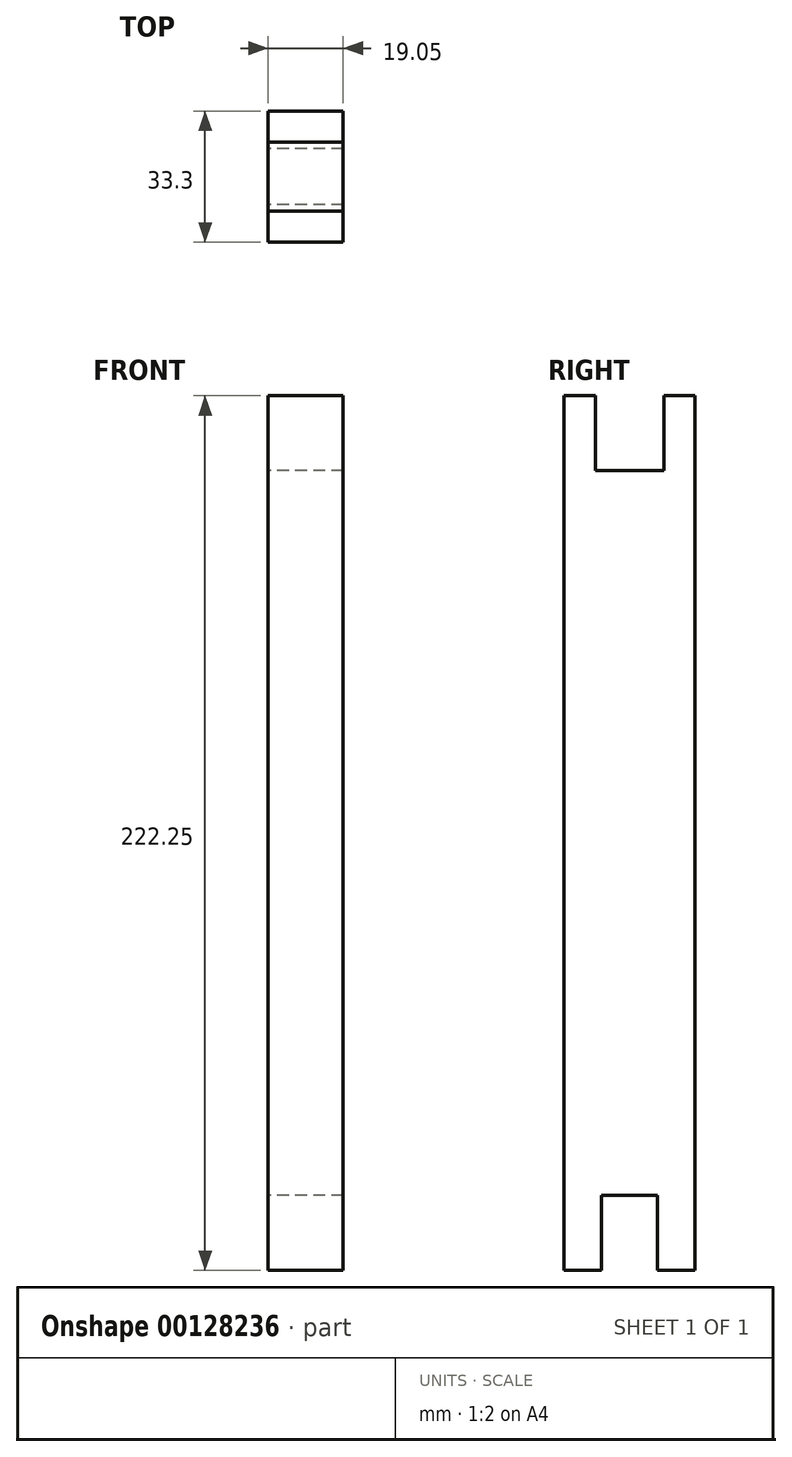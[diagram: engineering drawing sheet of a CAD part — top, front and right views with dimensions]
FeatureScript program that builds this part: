
annotation { "Feature Type Name" : "Feature", "Feature Type Description" : "" }
export const myFeature = defineFeature(function(context is Context, id is Id, definition is map)
    precondition{}
    {
        {
            var Q0;
            Q0=qCreatedBy(makeId("Right.planeOp"),FACE);
            var sketch = newSketch(context, id + "F0", { "sketchPlane" : qUnion([Q0])});
            skLineSegment(sketch, "E0", {"start": v(-50.77, 79.17) * mm, "end": v(-50.77, -143.08) * mm});
            skLineSegment(sketch, "E1", {"start": v(-50.77, 79.17) * mm, "end": v(-42.84, 79.17) * mm});
            skLineSegment(sketch, "E2", {"start": v(-42.84, 79.17) * mm, "end": v(-42.84, 60.12) * mm});
            skLineSegment(sketch, "E3", {"start": v(-42.84, 60.12) * mm, "end": v(-34.12, 60.12) * mm});
            skLineSegment(sketch, "E4", {"start": v(-50.77, -143.08) * mm, "end": v(-41.23, -143.08) * mm});
            skLineSegment(sketch, "E5", {"start": v(-41.23, -143.08) * mm, "end": v(-41.23, -124.03) * mm});
            skLineSegment(sketch, "E6", {"start": v(-41.23, -124.03) * mm, "end": v(-34.12, -124.03) * mm});
            skLineSegment(sketch, "E7", {"start": v(-34.12, 60.12) * mm, "end": v(-34.12, -124.03) * mm, "construction": true});
            skLineSegment(sketch, "E8.MirrorCS", {"start": v(-25.41, 60.12) * mm, "end": v(-34.12, 60.12) * mm});
            skLineSegment(sketch, "E9.MirrorCS", {"start": v(-25.41, 79.17) * mm, "end": v(-25.41, 60.12) * mm});
            skLineSegment(sketch, "E10.MirrorCS", {"start": v(-27.01, -124.03) * mm, "end": v(-34.12, -124.03) * mm});
            skLineSegment(sketch, "E11.MirrorCS", {"start": v(-27.01, -143.08) * mm, "end": v(-27.01, -124.03) * mm});
            skLineSegment(sketch, "E12.MirrorCS", {"start": v(-17.47, 79.17) * mm, "end": v(-17.47, -143.08) * mm});
            skLineSegment(sketch, "E13.MirrorCS", {"start": v(-17.47, 79.17) * mm, "end": v(-25.41, 79.17) * mm});
            skLineSegment(sketch, "E14.MirrorCS", {"start": v(-17.47, -143.08) * mm, "end": v(-27.01, -143.08) * mm});
            skSolve(sketch);
        }
        {
            var Q0;
            Q0=qSketchRegion(id+"F0",true);
            extrude(context, id + "F1", {"entities" : qUnion([Q0]), "depth" : 19.05 * mm});
        }
        {
            var Q0;
            Q0=qSketchRegion(id+"F0",true);
            extrude(context, id + "F2", {"entities" : qUnion([Q0]), "operationType" : NewBodyOperationType.ADD, "depth" : 9.52 * mm});
        }
    });
